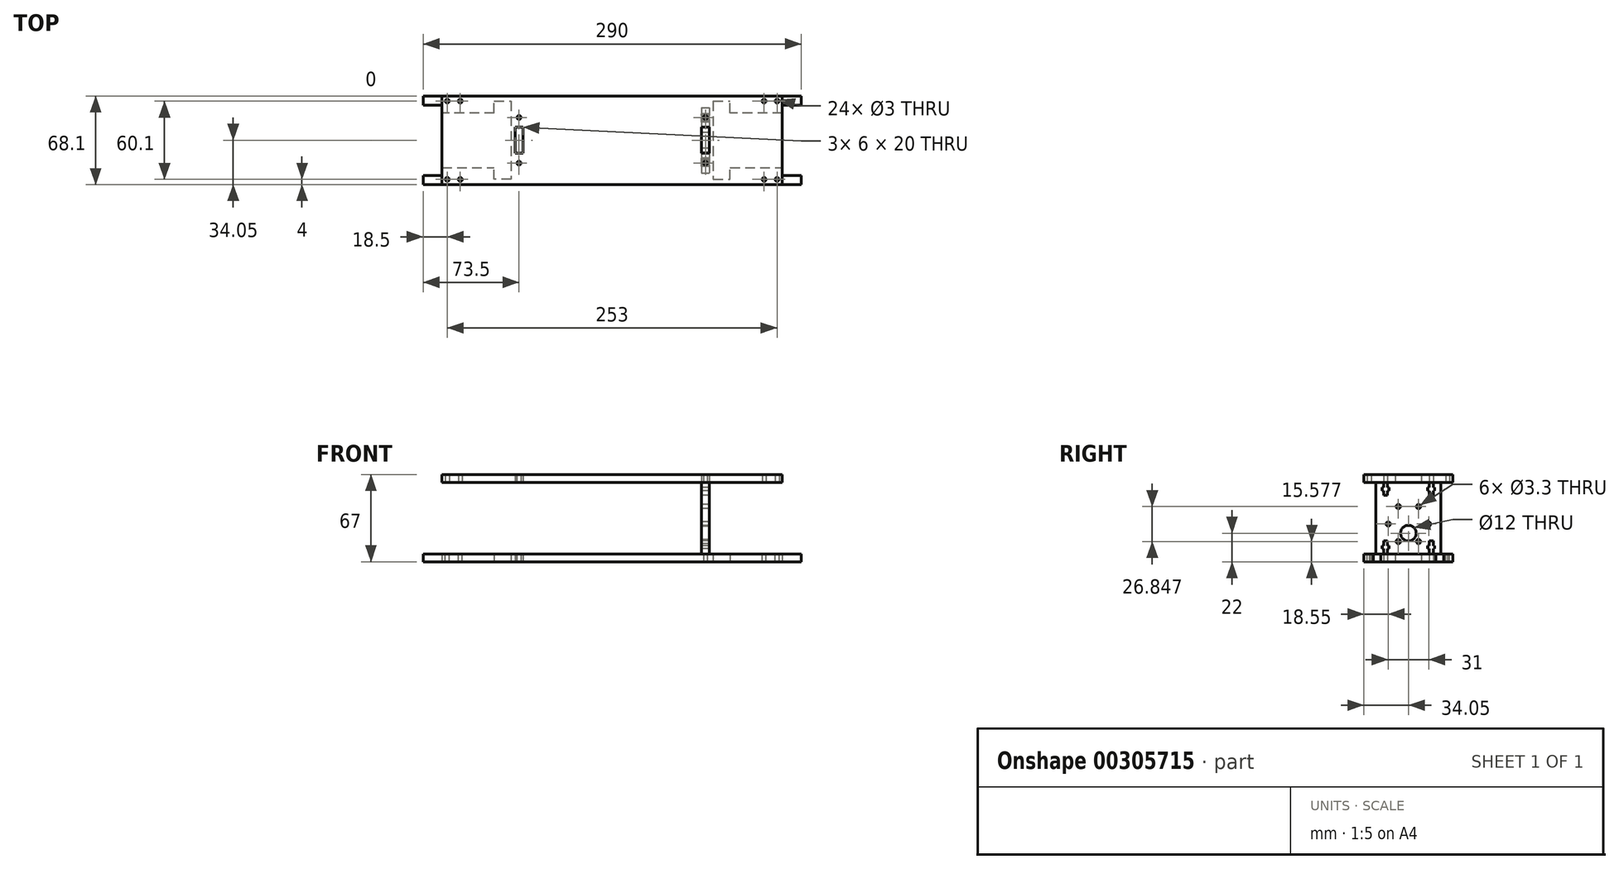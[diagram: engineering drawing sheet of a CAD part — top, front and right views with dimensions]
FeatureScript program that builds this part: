
annotation { "Feature Type Name" : "Feature", "Feature Type Description" : "" }
export const myFeature = defineFeature(function(context is Context, id is Id, definition is map)
    precondition{}
    {
        {
            var Q0;
            Q0=qCreatedBy(makeId("Top.planeOp"),FACE);
            var sketch = newSketch(context, id + "F0", { "sketchPlane" : qUnion([Q0])});
            skLineSegment(sketch, "E0.bottom", {"start": v(145, 34.05) * mm, "end": v(-145, 34.05) * mm});
            skLineSegment(sketch, "E0.top", {"start": v(145, -34.05) * mm, "end": v(-145, -34.05) * mm});
            skLineSegment(sketch, "E0.left", {"start": v(145, 34.05) * mm, "end": v(145, 27) * mm});
            skLineSegment(sketch, "E0.right", {"start": v(-145, 34.05) * mm, "end": v(-145, 27) * mm});
            skPoint(sketch, "E0.middle", {"position": v(0, 0) * mm});
            skPoint(sketch, "E1", {"position": v(126.5, -30.05) * mm});
            skPoint(sketch, "E2", {"position": v(116.5, -30.05) * mm});
            skPoint(sketch, "E3", {"position": v(126.5, 30.05) * mm});
            skPoint(sketch, "E4", {"position": v(116.5, 30.05) * mm});
            skPoint(sketch, "E5", {"position": v(-116.5, -30.05) * mm});
            skPoint(sketch, "E6", {"position": v(-126.5, -30.05) * mm});
            skPoint(sketch, "E7", {"position": v(-126.5, 30.05) * mm});
            skPoint(sketch, "E8", {"position": v(-116.5, 30.05) * mm});
            skLineSegment(sketch, "E9", {"start": v(130.5, 21) * mm, "end": v(90.5, 21) * mm});
            skLineSegment(sketch, "E10", {"start": v(90.5, 21) * mm, "end": v(90.5, -21) * mm, "construction": true});
            skLineSegment(sketch, "E11", {"start": v(90.5, -21) * mm, "end": v(130.5, -21) * mm});
            skLineSegment(sketch, "E12", {"start": v(130.5, -21) * mm, "end": v(130.5, -27) * mm});
            skLineSegment(sketch, "E13", {"start": v(130.5, -27) * mm, "end": v(145, -27) * mm});
            skLineSegment(sketch, "E14", {"start": v(130.5, 21) * mm, "end": v(130.5, 27) * mm});
            skLineSegment(sketch, "E15", {"start": v(130.5, 27) * mm, "end": v(145, 27) * mm});
            skLineSegment(sketch, "E16.trimOffspring", {"start": v(145, -27) * mm, "end": v(145, -34.05) * mm});
            skPoint(sketch, "E17", {"position": v(90.5, 0) * mm});
            skLineSegment(sketch, "E18", {"start": v(-145, -27) * mm, "end": v(-130.5, -27) * mm});
            skLineSegment(sketch, "E19", {"start": v(-130.5, -27) * mm, "end": v(-130.5, -21) * mm});
            skLineSegment(sketch, "E20", {"start": v(-130.5, -21) * mm, "end": v(-90.5, -21) * mm});
            skLineSegment(sketch, "E21", {"start": v(-90.5, 21) * mm, "end": v(-130.5, 21) * mm});
            skLineSegment(sketch, "E22", {"start": v(-130.5, 21) * mm, "end": v(-130.5, 27) * mm});
            skLineSegment(sketch, "E23", {"start": v(-130.5, 27) * mm, "end": v(-145, 27) * mm});
            skLineSegment(sketch, "E24.trimOffspring", {"start": v(-145, -27) * mm, "end": v(-145, -34.05) * mm});
            skLineSegment(sketch, "E25", {"start": v(68.5, 25) * mm, "end": v(68.5, -25) * mm, "construction": true});
            skPoint(sketch, "E26", {"position": v(68.5, 0) * mm});
            skLineSegment(sketch, "E27.bottom", {"start": v(74.5, 10) * mm, "end": v(68.5, 10) * mm});
            skLineSegment(sketch, "E27.top", {"start": v(74.5, -10) * mm, "end": v(68.5, -10) * mm});
            skLineSegment(sketch, "E27.left", {"start": v(74.5, 10) * mm, "end": v(74.5, -10) * mm});
            skLineSegment(sketch, "E27.right", {"start": v(68.5, 10) * mm, "end": v(68.5, -10) * mm});
            skCircle(sketch, "E28", {"center": v(71.5, 17.5) * mm, "radius": 1.5 * mm});
            skCircle(sketch, "E29", {"center": v(71.5, -17.5) * mm, "radius": 1.5 * mm});
            skLineSegment(sketch, "E30", {"start": v(71.5, 17.5) * mm, "end": v(71.5, -17.5) * mm, "construction": true});
            skPoint(sketch, "E31", {"position": v(71.5, 0) * mm});
            skLineSegment(sketch, "E32", {"start": v(68.5, 0) * mm, "end": v(74.5, 0) * mm, "construction": true});
            skLineSegment(sketch, "E33.bottom", {"start": v(-74.5, 10) * mm, "end": v(-68.5, 10) * mm});
            skLineSegment(sketch, "E33.top", {"start": v(-74.5, -10) * mm, "end": v(-68.5, -10) * mm});
            skLineSegment(sketch, "E33.left", {"start": v(-74.5, 10) * mm, "end": v(-74.5, -10) * mm});
            skLineSegment(sketch, "E33.right", {"start": v(-68.5, 10) * mm, "end": v(-68.5, -10) * mm});
            skCircle(sketch, "E34", {"center": v(-71.5, 17.5) * mm, "radius": 1.5 * mm});
            skCircle(sketch, "E35", {"center": v(-71.5, -17.5) * mm, "radius": 1.5 * mm});
            skLineSegment(sketch, "E36.bottom", {"start": v(77.5, 30) * mm, "end": v(90.5, 30) * mm});
            skLineSegment(sketch, "E36.top", {"start": v(77.5, -30) * mm, "end": v(90.5, -30) * mm});
            skLineSegment(sketch, "E36.left", {"start": v(77.5, 30) * mm, "end": v(77.5, -30) * mm});
            skLineSegment(sketch, "E37", {"start": v(90.5, -30) * mm, "end": v(90.5, -21) * mm});
            skLineSegment(sketch, "E38", {"start": v(90.5, 21) * mm, "end": v(90.5, 30) * mm});
            skLineSegment(sketch, "E39", {"start": v(-90.5, 21) * mm, "end": v(-90.5, 30) * mm});
            skLineSegment(sketch, "E40", {"start": v(-90.5, 30) * mm, "end": v(-77.5, 30) * mm});
            skLineSegment(sketch, "E41", {"start": v(-77.5, 30) * mm, "end": v(-77.5, -30) * mm});
            skLineSegment(sketch, "E42", {"start": v(-77.5, -30) * mm, "end": v(-90.5, -30) * mm});
            skLineSegment(sketch, "E43", {"start": v(-90.5, -30) * mm, "end": v(-90.5, -21) * mm});
            skSolve(sketch);
        }
        {
            var Q0;
            Q0 = qSketchRegion(id + "F0", true);
            extrude(context, id + "F1", {"entities" : qUnion([Q0]), "depth" : 6 * mm});
        }
        {
            var Q0;
            Q0=sQuery(id+"F0.wireOp",VERTEX,"E1");
            var Q1;
            Q1=sQuery(id+"F0.wireOp",VERTEX,"E2");
            var Q2;
            Q2=sQuery(id+"F0.wireOp",VERTEX,"E3");
            var Q3;
            Q3=sQuery(id+"F0.wireOp",VERTEX,"E4");
            var Q4;
            Q4=sQuery(id+"F0.wireOp",VERTEX,"E5");
            var Q5;
            Q5=sQuery(id+"F0.wireOp",VERTEX,"E6");
            var Q6;
            Q6=sQuery(id+"F0.wireOp",VERTEX,"E8");
            var Q7;
            Q7=sQuery(id+"F0.wireOp",VERTEX,"E7");
            var Q8;
            Q8=makeQuery(id+"F1.opExtrude","SWEPT_BODY",BODY,{"disambiguationData":[OSD([sQuery(id+"F0.wireOp",EDGE,"E0.bottom"),sQuery(id+"F0.wireOp",EDGE,"E0.top"),sQuery(id+"F0.wireOp",EDGE,"E0.left"),sQuery(id+"F0.wireOp",EDGE,"E0.right")])]});
            hole(context, id + "F2", {"style" : HoleStyle.SIMPLE, "endStyle" : HoleEndStyle.THROUGH, "oppositeDirection" : true, "standardTappedOrClearance" : lookupTablePath({ "standard" : "ISO", "size" : "3", "type" : "Drilled" }), "standardBlindInLast" : lookupTablePath({ "standard" : "ISO", "size" : "3", "type" : "Drilled" }), "holeDiameter" : 3 * mm, "tappedDepth" : 10.9 * mm, "tapClearance" : 3, "locations" : qUnion([Q0, Q1, Q2, Q3, Q4, Q5, Q6, Q7]), "scope" : qUnion([Q8])});
        }
        {
            var Q0;
            Q0=makeQuery(id+"F1.opExtrude","CAP_FACE",FACE,{"disambiguationData":[OSD([sQuery(id+"F0.wireOp",EDGE,"E0.bottom"),sQuery(id+"F0.wireOp",EDGE,"E0.top"),sQuery(id+"F0.wireOp",EDGE,"E0.left"),sQuery(id+"F0.wireOp",EDGE,"E0.right"),sQuery(id+"F0.wireOp",EDGE,"E9"),sQuery(id+"F0.wireOp",EDGE,"E10"),sQuery(id+"F0.wireOp",EDGE,"E11"),sQuery(id+"F0.wireOp",EDGE,"E12"),sQuery(id+"F0.wireOp",EDGE,"E13"),sQuery(id+"F0.wireOp",EDGE,"E14"),sQuery(id+"F0.wireOp",EDGE,"E15"),sQuery(id+"F0.wireOp",EDGE,"E16.trimOffspring"),sQuery(id+"F0.wireOp",EDGE,"E18"),sQuery(id+"F0.wireOp",EDGE,"E19"),sQuery(id+"F0.wireOp",EDGE,"E20"),sQuery(id+"F0.wireOp",EDGE,"jEcUEht7-0Wzt-mQMa-QwQx-0Txn2W36VDiV"),sQuery(id+"F0.wireOp",EDGE,"E21"),sQuery(id+"F0.wireOp",EDGE,"E22"),sQuery(id+"F0.wireOp",EDGE,"E23"),sQuery(id+"F0.wireOp",EDGE,"E24.trimOffspring")])],"isStart":false});
            var sketch = newSketch(context, id + "F3", { "sketchPlane" : qUnion([Q0])});
            skLineSegment(sketch, "E44.bottom", {"start": v(68.5, 25) * mm, "end": v(74.5, 25) * mm});
            skLineSegment(sketch, "E44.top", {"start": v(68.5, -25) * mm, "end": v(74.5, -25) * mm});
            skLineSegment(sketch, "E44.left", {"start": v(68.5, 25) * mm, "end": v(68.5, -25) * mm});
            skLineSegment(sketch, "E44.right", {"start": v(74.5, 25) * mm, "end": v(74.5, -25) * mm});
            skSolve(sketch);
        }
        {
            var Q0;
            Q0 = qSketchRegion(id + "F3", true);
            extrude(context, id + "F4", {"entities" : qUnion([Q0]), "depth" : 55 * mm});
        }
        {
            var Q0;
            Q0=makeQuery(id+"F4.opExtrude","CAP_FACE",FACE,{"disambiguationData":[OSD([sQuery(id+"F3.wireOp",EDGE,"E44.bottom"),sQuery(id+"F3.wireOp",EDGE,"E44.top"),sQuery(id+"F3.wireOp",EDGE,"E44.left"),sQuery(id+"F3.wireOp",EDGE,"E44.right")])],"isStart":true});
            var sketch = newSketch(context, id + "F5", { "sketchPlane" : qUnion([Q0])});
            skLineSegment(sketch, "E45.bottom", {"start": v(74.5, -10) * mm, "end": v(68.5, -10) * mm});
            skLineSegment(sketch, "E45.top", {"start": v(74.5, 10) * mm, "end": v(68.5, 10) * mm});
            skLineSegment(sketch, "E45.left", {"start": v(74.5, -10) * mm, "end": v(74.5, 10) * mm});
            skLineSegment(sketch, "E45.right", {"start": v(68.5, -10) * mm, "end": v(68.5, 10) * mm});
            skSolve(sketch);
        }
        {
            var Q0;
            Q0 = qSketchRegion(id + "F5", true);
            extrude(context, id + "F6", {"entities" : qUnion([Q0]), "operationType" : NewBodyOperationType.ADD, "depth" : 6 * mm});
        }
        {
            var Q0;
            Q0=makeQuery(id+"F4.opExtrude","SWEPT_FACE",FACE,{"disambiguationData":[OSD([sQuery(id+"F3.wireOp",EDGE,"E44.left")])]});
            var sketch = newSketch(context, id + "F7", { "sketchPlane" : qUnion([Q0])});
            skCircle(sketch, "E46", {"center": v(0, 29) * mm, "radius": 15.5 * mm, "construction": true});
            skCircle(sketch, "E47", {"center": v(0, 22) * mm, "radius": 6 * mm});
            skCircle(sketch, "E48", {"center": v(7.75, 15.58) * mm, "radius": 1.65 * mm});
            skCircle(sketch, "E49", {"center": v(15.5, 29) * mm, "radius": 1.65 * mm});
            skCircle(sketch, "E50", {"center": v(7.75, 42.42) * mm, "radius": 1.65 * mm});
            skCircle(sketch, "E51", {"center": v(-7.75, 42.42) * mm, "radius": 1.65 * mm});
            skCircle(sketch, "E52", {"center": v(-15.5, 29) * mm, "radius": 1.65 * mm});
            skCircle(sketch, "E53", {"center": v(-7.75, 15.58) * mm, "radius": 1.65 * mm});
            skLineSegment(sketch, "E54", {"start": v(-7.75, 15.58) * mm, "end": v(0, 29) * mm, "construction": true});
            skLineSegment(sketch, "E55", {"start": v(7.75, 15.58) * mm, "end": v(0, 29) * mm, "construction": true});
            skLineSegment(sketch, "E56", {"start": v(0, 29) * mm, "end": v(15.5, 29) * mm, "construction": true});
            skLineSegment(sketch, "E57", {"start": v(0, 29) * mm, "end": v(7.75, 42.42) * mm, "construction": true});
            skLineSegment(sketch, "E58", {"start": v(0, 29) * mm, "end": v(-7.75, 42.42) * mm, "construction": true});
            skLineSegment(sketch, "E59", {"start": v(0, 29) * mm, "end": v(-15.5, 29) * mm, "construction": true});
            skSolve(sketch);
        }
        {
            var Q0;
            Q0 = qSketchRegion(id + "F7", true);
            extrude(context, id + "F8", {"entities" : qUnion([Q0]), "operationType" : NewBodyOperationType.REMOVE, "endBound" : BoundingType.UP_TO_NEXT, "oppositeDirection" : true, "depth" : 25 * mm});
        }
        {
            var Q0;
            Q0=makeQuery(id+"F6.boolean.opBoolean","MERGE",FACE,{"derivedFrom":[makeQuery(id+"F4.opExtrude","SWEPT_FACE",FACE,{"disambiguationData":[OSD([sQuery(id+"F3.wireOp",EDGE,"E44.left")])]}),makeQuery(id+"F6.opExtrude","SWEPT_FACE",FACE,{"disambiguationData":[OSD([sQuery(id+"F5.wireOp",EDGE,"E45.right")])]})]});
            var sketch = newSketch(context, id + "F9", { "sketchPlane" : qUnion([Q0])});
            skLineSegment(sketch, "E60", {"start": v(19, 6) * mm, "end": v(19, 10) * mm});
            skLineSegment(sketch, "E61", {"start": v(19, 10) * mm, "end": v(20.2, 10) * mm});
            skLineSegment(sketch, "E62", {"start": v(20.2, 10) * mm, "end": v(20.2, 12.3) * mm});
            skLineSegment(sketch, "E63", {"start": v(20.2, 12.3) * mm, "end": v(19, 12.3) * mm});
            skLineSegment(sketch, "E64", {"start": v(19, 12.3) * mm, "end": v(19, 16) * mm});
            skLineSegment(sketch, "E65", {"start": v(19, 16) * mm, "end": v(16, 16) * mm});
            skLineSegment(sketch, "E66", {"start": v(16, 16) * mm, "end": v(16, 12.3) * mm});
            skLineSegment(sketch, "E67", {"start": v(16, 12.3) * mm, "end": v(14.8, 12.3) * mm});
            skLineSegment(sketch, "E68", {"start": v(14.8, 12.3) * mm, "end": v(14.8, 10) * mm});
            skLineSegment(sketch, "E69", {"start": v(14.8, 10) * mm, "end": v(16, 10) * mm});
            skLineSegment(sketch, "E70", {"start": v(16, 10) * mm, "end": v(16, 6) * mm});
            skLineSegment(sketch, "E71", {"start": v(16, 6) * mm, "end": v(19, 6) * mm});
            skPoint(sketch, "E72", {"position": v(17.5, 16) * mm});
            skLineSegment(sketch, "E73", {"start": v(-19, 6) * mm, "end": v(-19, 10) * mm});
            skLineSegment(sketch, "E74", {"start": v(-19, 10) * mm, "end": v(-20.2, 10) * mm});
            skLineSegment(sketch, "E75", {"start": v(-20.2, 10) * mm, "end": v(-20.2, 12.3) * mm});
            skLineSegment(sketch, "E76", {"start": v(-20.2, 12.3) * mm, "end": v(-19, 12.3) * mm});
            skLineSegment(sketch, "E77", {"start": v(-19, 12.3) * mm, "end": v(-19, 16) * mm});
            skLineSegment(sketch, "E78", {"start": v(-19, 16) * mm, "end": v(-16, 16) * mm});
            skLineSegment(sketch, "E79", {"start": v(-16, 16) * mm, "end": v(-16, 12.3) * mm});
            skLineSegment(sketch, "E80", {"start": v(-16, 12.3) * mm, "end": v(-14.8, 12.3) * mm});
            skLineSegment(sketch, "E81", {"start": v(-14.8, 12.3) * mm, "end": v(-14.8, 10) * mm});
            skLineSegment(sketch, "E82", {"start": v(-14.8, 10) * mm, "end": v(-16, 10) * mm});
            skLineSegment(sketch, "E83", {"start": v(-16, 10) * mm, "end": v(-16, 6) * mm});
            skLineSegment(sketch, "E84", {"start": v(-16, 6) * mm, "end": v(-19, 6) * mm});
            skLineSegment(sketch, "E85", {"start": v(25, 33.5) * mm, "end": v(-25, 33.5) * mm, "construction": true});
            skLineSegment(sketch, "E86", {"start": v(16, 61) * mm, "end": v(19, 61) * mm});
            skLineSegment(sketch, "E87", {"start": v(19, 61) * mm, "end": v(19, 57) * mm});
            skLineSegment(sketch, "E88", {"start": v(19, 57) * mm, "end": v(20.2, 57) * mm});
            skLineSegment(sketch, "E89", {"start": v(20.2, 57) * mm, "end": v(20.2, 54.7) * mm});
            skLineSegment(sketch, "E90", {"start": v(20.2, 54.7) * mm, "end": v(19, 54.7) * mm});
            skLineSegment(sketch, "E91", {"start": v(19, 54.7) * mm, "end": v(19, 51) * mm});
            skLineSegment(sketch, "E92", {"start": v(19, 51) * mm, "end": v(16, 51) * mm});
            skLineSegment(sketch, "E93", {"start": v(16, 51) * mm, "end": v(16, 54.7) * mm});
            skLineSegment(sketch, "E94", {"start": v(16, 54.7) * mm, "end": v(14.8, 54.7) * mm});
            skLineSegment(sketch, "E95", {"start": v(14.8, 54.7) * mm, "end": v(14.8, 57) * mm});
            skLineSegment(sketch, "E96", {"start": v(14.8, 57) * mm, "end": v(16, 57) * mm});
            skLineSegment(sketch, "E97", {"start": v(16, 57) * mm, "end": v(16, 61) * mm});
            skLineSegment(sketch, "E98", {"start": v(-19, 61) * mm, "end": v(-16, 61) * mm});
            skLineSegment(sketch, "E99", {"start": v(-16, 61) * mm, "end": v(-16, 57) * mm});
            skLineSegment(sketch, "E100", {"start": v(-16, 57) * mm, "end": v(-14.8, 57) * mm});
            skLineSegment(sketch, "E101", {"start": v(-14.8, 57) * mm, "end": v(-14.8, 54.7) * mm});
            skLineSegment(sketch, "E102", {"start": v(-14.8, 54.7) * mm, "end": v(-16, 54.7) * mm});
            skLineSegment(sketch, "E103", {"start": v(-16, 54.7) * mm, "end": v(-16, 51) * mm});
            skLineSegment(sketch, "E104", {"start": v(-16, 51) * mm, "end": v(-19, 51) * mm});
            skLineSegment(sketch, "E105", {"start": v(-19, 51) * mm, "end": v(-19, 54.7) * mm});
            skLineSegment(sketch, "E106", {"start": v(-19, 54.7) * mm, "end": v(-20.2, 54.7) * mm});
            skLineSegment(sketch, "E107", {"start": v(-20.2, 54.7) * mm, "end": v(-20.2, 57) * mm});
            skLineSegment(sketch, "E108", {"start": v(-20.2, 57) * mm, "end": v(-19, 57) * mm});
            skLineSegment(sketch, "E109", {"start": v(-19, 57) * mm, "end": v(-19, 61) * mm});
            skSolve(sketch);
        }
        {
            var Q0;
            Q0 = qSketchRegion(id + "F9", true);
            extrude(context, id + "F10", {"entities" : qUnion([Q0]), "operationType" : NewBodyOperationType.REMOVE, "endBound" : BoundingType.UP_TO_NEXT, "oppositeDirection" : true, "depth" : 25 * mm});
        }
        {
            var Q0;
            {var subQ0=sQuery(id+"F3.wireOp",EDGE,"E44.right");var subQ1=sQuery(id+"F3.wireOp",EDGE,"E44.left");Q0=makeQuery(id+"F10.boolean.opBoolean","SPLIT",FACE,{"disambiguationData":[TD([makeQuery(id+"F10.opExtrude","SWEPT_FACE",FACE,{"disambiguationData":[OSD([sQuery(id+"F9.wireOp",EDGE,"E97")])]})])],"derivedFrom":makeQuery(id+"F4.opExtrude","CAP_FACE",FACE,{"disambiguationData":[OSD([sQuery(id+"F3.wireOp",EDGE,"E44.bottom"),sQuery(id+"F3.wireOp",EDGE,"E44.top"),subQ1,subQ0])],"isStart":false})});}
            var sketch = newSketch(context, id + "F11", { "sketchPlane" : qUnion([Q0])});
            skLineSegment(sketch, "E110.bottom", {"start": v(68.5, 10) * mm, "end": v(74.5, 10) * mm});
            skLineSegment(sketch, "E110.top", {"start": v(68.5, -10) * mm, "end": v(74.5, -10) * mm});
            skLineSegment(sketch, "E110.left", {"start": v(68.5, 10) * mm, "end": v(68.5, -10) * mm});
            skLineSegment(sketch, "E110.right", {"start": v(74.5, 10) * mm, "end": v(74.5, -10) * mm});
            skSolve(sketch);
        }
        {
            var Q0;
            Q0 = qSketchRegion(id + "F11", true);
            extrude(context, id + "F12", {"entities" : qUnion([Q0]), "operationType" : NewBodyOperationType.ADD, "depth" : 6 * mm});
        }
        {
            var Q0;
            {var subQ2=sQuery(id+"F3.wireOp",EDGE,"E44.right");var subQ4=sQuery(id+"F3.wireOp",EDGE,"E44.left");var subQ6=makeQuery(id+"F10.opExtrude","SWEPT_FACE",FACE,{"disambiguationData":[OSD([sQuery(id+"F9.wireOp",EDGE,"E99")])]});Q0=makeQuery(id+"F12.boolean.opBoolean","SPLIT",FACE,{"disambiguationData":[TD([makeQuery(id+"F10.boolean.opBoolean","COPY",FACE,{"derivedFrom":subQ6})])],"derivedFrom":makeQuery(id+"F10.boolean.opBoolean","SPLIT",FACE,{"disambiguationData":[TD([makeQuery(id+"F10.opExtrude","SWEPT_FACE",FACE,{"disambiguationData":[OSD([sQuery(id+"F9.wireOp",EDGE,"E97")])]})])],"derivedFrom":makeQuery(id+"F4.opExtrude","CAP_FACE",FACE,{"disambiguationData":[OSD([sQuery(id+"F3.wireOp",EDGE,"E44.bottom"),sQuery(id+"F3.wireOp",EDGE,"E44.top"),subQ4,subQ2])],"isStart":false})})});}
            var sketch = newSketch(context, id + "F13", { "sketchPlane" : qUnion([Q0])});
            skLineSegment(sketch, "E111.bottom", {"start": v(-130.5, 34.05) * mm, "end": v(130.5, 34.05) * mm});
            skLineSegment(sketch, "E111.top", {"start": v(-130.5, -34.05) * mm, "end": v(130.5, -34.05) * mm});
            skLineSegment(sketch, "E111.left", {"start": v(-130.5, 34.05) * mm, "end": v(-130.5, -34.05) * mm});
            skLineSegment(sketch, "E111.right", {"start": v(130.5, 34.05) * mm, "end": v(130.5, -34.05) * mm});
            skLineSegment(sketch, "E112.bottom", {"start": v(68.5, 10) * mm, "end": v(74.5, 10) * mm});
            skLineSegment(sketch, "E112.top", {"start": v(68.5, -10) * mm, "end": v(74.5, -10) * mm});
            skLineSegment(sketch, "E112.left", {"start": v(68.5, 10) * mm, "end": v(68.5, -10) * mm});
            skLineSegment(sketch, "E112.right", {"start": v(74.5, 10) * mm, "end": v(74.5, -10) * mm});
            skLineSegment(sketch, "E113", {"start": v(0, 34.05) * mm, "end": v(0, -34.05) * mm, "construction": true});
            skLineSegment(sketch, "E114.bottom", {"start": v(-74.5, 10) * mm, "end": v(-68.5, 10) * mm});
            skLineSegment(sketch, "E114.top", {"start": v(-74.5, -10) * mm, "end": v(-68.5, -10) * mm});
            skLineSegment(sketch, "E114.left", {"start": v(-74.5, 10) * mm, "end": v(-74.5, -10) * mm});
            skLineSegment(sketch, "E114.right", {"start": v(-68.5, 10) * mm, "end": v(-68.5, -10) * mm});
            skCircle(sketch, "E115", {"center": v(-71.5, 17.5) * mm, "radius": 1.5 * mm});
            skCircle(sketch, "E116", {"center": v(-71.5, -17.5) * mm, "radius": 1.5 * mm});
            skCircle(sketch, "E117", {"center": v(-126.5, 30.05) * mm, "radius": 1.5 * mm});
            skCircle(sketch, "E118", {"center": v(-116.5, 30.05) * mm, "radius": 1.5 * mm});
            skCircle(sketch, "E119", {"center": v(-126.5, -30.05) * mm, "radius": 1.5 * mm});
            skCircle(sketch, "E120", {"center": v(-116.5, -30.05) * mm, "radius": 1.5 * mm});
            skCircle(sketch, "E121", {"center": v(116.5, -30.05) * mm, "radius": 1.5 * mm});
            skCircle(sketch, "E122", {"center": v(126.5, -30.05) * mm, "radius": 1.5 * mm});
            skCircle(sketch, "E123", {"center": v(116.5, 30.05) * mm, "radius": 1.5 * mm});
            skCircle(sketch, "E124", {"center": v(126.5, 30.05) * mm, "radius": 1.5 * mm});
            skCircle(sketch, "E125", {"center": v(71.5, -17.5) * mm, "radius": 1.5 * mm});
            skCircle(sketch, "E126", {"center": v(71.5, 17.5) * mm, "radius": 1.5 * mm});
            skSolve(sketch);
        }
        {
            var Q0;
            Q0 = qSketchRegion(id + "F13", true);
            extrude(context, id + "F14", {"entities" : qUnion([Q0]), "depth" : 6 * mm});
        }
    });
